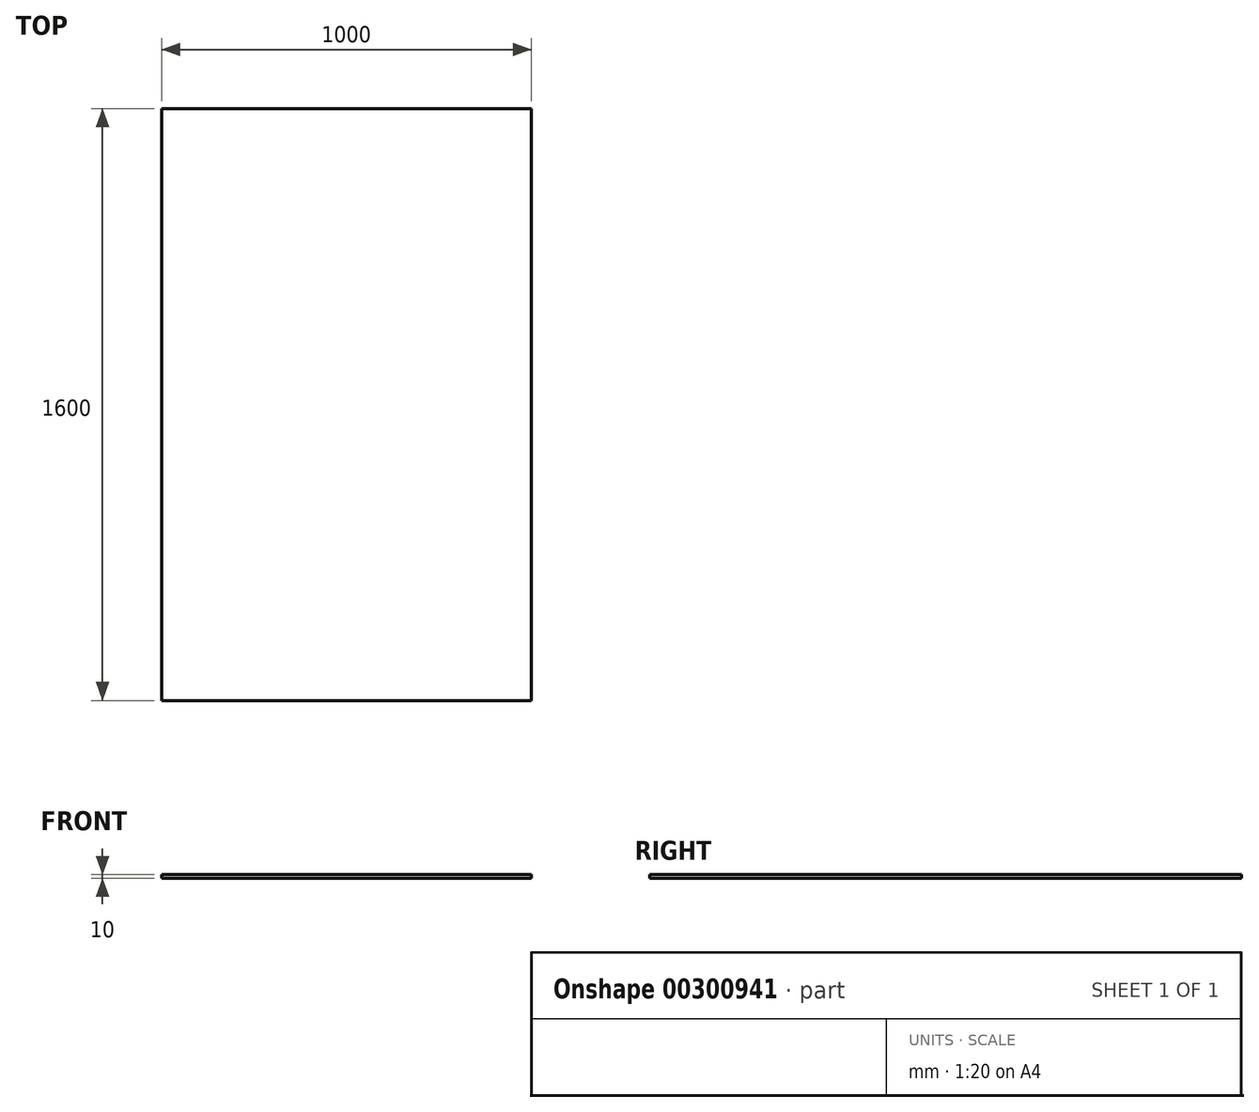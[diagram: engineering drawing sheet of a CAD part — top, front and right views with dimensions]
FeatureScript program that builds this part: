
annotation { "Feature Type Name" : "Feature", "Feature Type Description" : "" }
export const myFeature = defineFeature(function(context is Context, id is Id, definition is map)
    precondition{}
    {
        {
            var Q0;
            Q0=qCreatedBy(makeId("Top.planeOp"),FACE);
            var sketch = newSketch(context, id + "F0", { "sketchPlane" : qUnion([Q0])});
            skLineSegment(sketch, "E0", {"start": v(0, 0) * mm, "end": v(1000, 0) * mm});
            skLineSegment(sketch, "E1", {"start": v(1000, 0) * mm, "end": v(1000, 1600) * mm});
            skLineSegment(sketch, "E2", {"start": v(1000, 1600) * mm, "end": v(0, 1600) * mm});
            skLineSegment(sketch, "E3", {"start": v(0, 1600) * mm, "end": v(0, 0) * mm});
            skSolve(sketch);
        }
        {
            var Q0;
            Q0=makeQuery(id+"F0.imprint","IMPRINT",FACE,{"disambiguationData":[TD([[makeQuery(id+"F0.imprint","IMPRINT",EDGE,{"derivedFrom":sQuery(id+"F0.wireOp",EDGE,"E0")}),1.0]])]});
            extrude(context, id + "F1", {"entities" : qUnion([Q0]), "oppositeDirection" : true, "depth" : 10 * mm});
        }
    });
